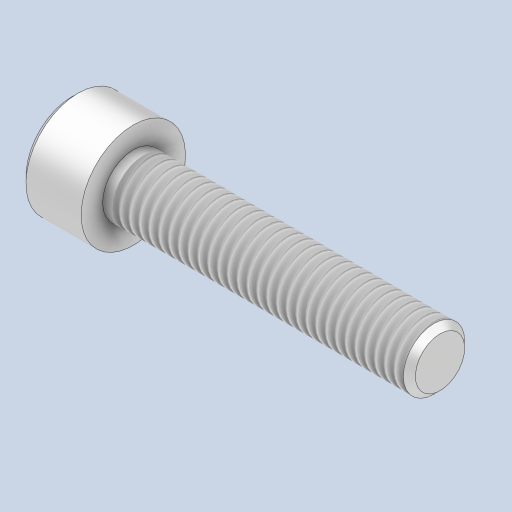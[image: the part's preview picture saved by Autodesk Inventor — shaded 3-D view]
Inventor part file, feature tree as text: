
AUTODESK INVENTOR PART (.ipt)
format: ipt  version: 2023 (Build 270158000, 158)  size: 194,048 bytes
history: native  units: mm
features: other x14, sketch x3, revolve x1, thread x1, hole x1, extrude x1
ambient origin geometry x8: Origin, YZ Plane, XZ Plane, XY Plane, X Axis, Y Axis, Z Axis, Center Point
bodies: Solid1 (feature_tree)
feature tree (21):
  revolve  "Revolution1"  [1 undecoded]
  thread  "Thread1"  [1 undecoded]
  hole  "Hole1"  [1 undecoded]
  extrude  "Extrusion1"  [1 undecoded]
  other  "bolt_XY"
  other  "bolt_YZ"
  other  "bolt_ZX"
  other  "bolt_X"
  other  "bolt_Y"
  other  "bolt_Z"
  other  "bolt_Center"
  other  "nut_XY"
  other  "nut_YZ"
  other  "nut_ZX"
  other  "nut_X"
  other  "nut_Y"
  other  "nut_Z"
  other  "nut_Center"
  sketch  "Sketch_1"  dims[d0=360.0deg d1=24.2mm d2=0.8mm]
  sketch  "Sketch2"  dims[d3=4.0mm d4=6.0mm d5=4.0mm d6=2.0mm d7=90.0deg d8=2.5mm d9=150.0deg d10=2.5mm d11=0.0mm]
  sketch  "Sketch_3"  dims[d12=0.0mm d13=0.0mm]
note: 4 required parameter values undecoded (feature->parameter linkage not recoverable at this tier; creation-order binding heuristic only, values carry confidence <= 0.55)